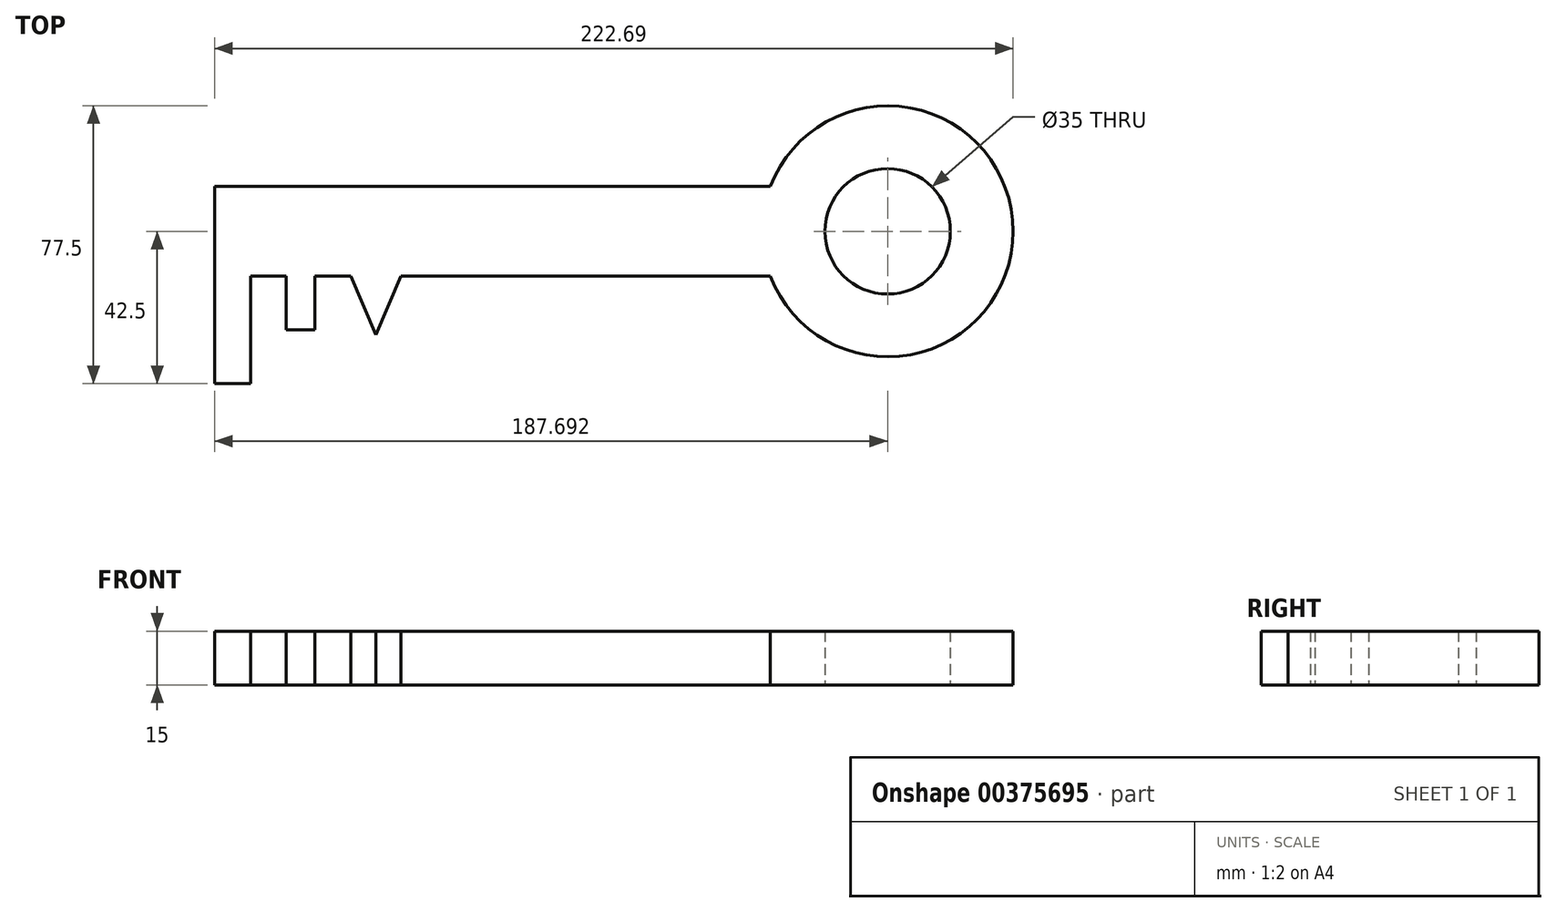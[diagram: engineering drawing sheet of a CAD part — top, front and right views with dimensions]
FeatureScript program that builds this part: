
annotation { "Feature Type Name" : "Feature", "Feature Type Description" : "" }
export const myFeature = defineFeature(function(context is Context, id is Id, definition is map)
    precondition{}
    {
        {
            var Q0;
            Q0=qCreatedBy(makeId("Top.planeOp"),FACE);
            var sketch = newSketch(context, id + "F0", { "sketchPlane" : qUnion([Q0])});
            skLineSegment(sketch, "E0.bottom", {"start": v(-105.23, 41.32) * mm, "end": v(49.77, 41.32) * mm});
            skLineSegment(sketch, "E0.top", {"start": v(-105.23, 16.32) * mm, "end": v(49.77, 16.32) * mm});
            skLineSegment(sketch, "E0.left", {"start": v(-105.23, 41.32) * mm, "end": v(-105.23, 16.32) * mm});
            skLineSegment(sketch, "E0.right", {"start": v(49.77, 41.32) * mm, "end": v(49.77, 16.32) * mm});
            skLineSegment(sketch, "E1.bottom", {"start": v(-105.23, 16.32) * mm, "end": v(-95.23, 16.32) * mm});
            skLineSegment(sketch, "E1.top", {"start": v(-105.23, -13.68) * mm, "end": v(-95.23, -13.68) * mm});
            skLineSegment(sketch, "E1.left", {"start": v(-105.23, 16.32) * mm, "end": v(-105.23, -13.68) * mm});
            skLineSegment(sketch, "E1.right", {"start": v(-95.23, 16.32) * mm, "end": v(-95.23, -13.68) * mm});
            skLineSegment(sketch, "E2.bottom", {"start": v(-85.23, 16.32) * mm, "end": v(-77.23, 16.32) * mm});
            skLineSegment(sketch, "E2.top", {"start": v(-85.23, 1.32) * mm, "end": v(-77.23, 1.32) * mm});
            skLineSegment(sketch, "E2.left", {"start": v(-85.23, 16.32) * mm, "end": v(-85.23, 1.32) * mm});
            skLineSegment(sketch, "E2.right", {"start": v(-77.23, 16.32) * mm, "end": v(-77.23, 1.32) * mm});
            skLineSegment(sketch, "E3", {"start": v(-67.23, 16.32) * mm, "end": v(-60.23, 0) * mm});
            skLineSegment(sketch, "E4", {"start": v(-60.23, 0) * mm, "end": v(-53.23, 16.32) * mm});
            skArc(sketch, "E5", {"start": v(49.77, 16.32) * mm, "mid": v(117.46, 28.82) * mm, "end": v(49.77, 41.32) * mm});
            skCircle(sketch, "E6", {"center": v(82.46, 28.82) * mm, "radius": 17.5 * mm});
            skLineSegment(sketch, "E7", {"start": v(82.46, 28.82) * mm, "end": v(-105.23, 28.82) * mm, "construction": true});
            skSolve(sketch);
        }
        {
            var Q0;
            Q0 = qSketchRegion(id + "F0", true);
            extrude(context, id + "F1", {"entities" : qUnion([Q0]), "depth" : 15 * mm});
        }
    });
